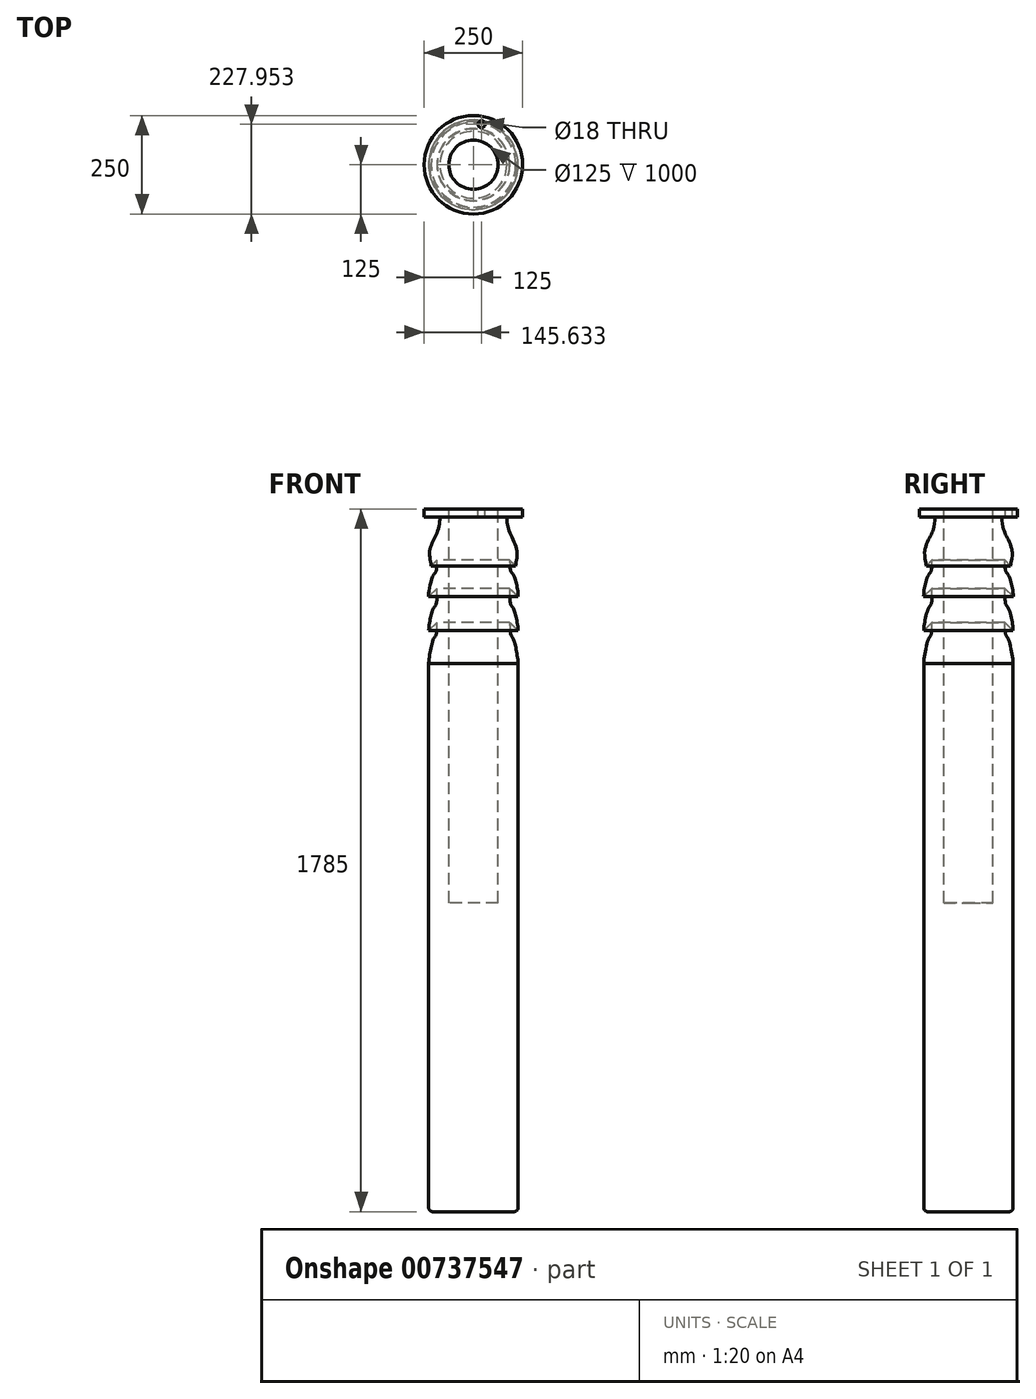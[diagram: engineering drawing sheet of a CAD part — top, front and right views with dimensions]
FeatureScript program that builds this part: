
annotation { "Feature Type Name" : "Feature", "Feature Type Description" : "" }
export const myFeature = defineFeature(function(context is Context, id is Id, definition is map)
    precondition{}
    {
        {
            var Q0;
            Q0=qCreatedBy(makeId("Front.planeOp"),FACE);
            var sketch = newSketch(context, id + "F0", { "sketchPlane" : qUnion([Q0])});
            skLineSegment(sketch, "E0", {"start": v(0, 1000) * mm, "end": v(0, -1000) * mm, "construction": true});
            skLineSegment(sketch, "E1", {"start": v(0, 796) * mm, "end": v(125, 796) * mm});
            skLineSegment(sketch, "E2", {"start": v(125, 796) * mm, "end": v(125, 776) * mm});
            skLineSegment(sketch, "E3", {"start": v(125, 776) * mm, "end": v(85, 776) * mm});
            skFitSpline(sketch, "E4", {"points": [v(85, 776) * mm, v(90.3, 741.64) * mm, v(110.68, 691.75) * mm, v(107.26, 651.86) * mm], "startDerivative": vector(5.14, -104) * mm, "endDerivative": vector(-8.82, -99.6) * mm});
            skFitSpline(sketch, "E5", {"points": [v(92.17, 666.19) * mm, v(100.58, 630.26) * mm, v(113.89, 573.44) * mm], "startDerivative": vector(5.42, -233.9) * mm, "endDerivative": vector(1.67, -111.03) * mm});
            skFitSpline(sketch, "E6", {"points": [v(92.17, 594.06) * mm, v(100.58, 545.8) * mm, v(113.58, 487.63) * mm], "startDerivative": vector(-2.08, -300.06) * mm, "endDerivative": vector(4.8, -112.09) * mm});
            skFitSpline(sketch, "E7", {"points": [v(92.17, 507.95) * mm, v(100.58, 467.82) * mm, v(113.58, 404) * mm], "startDerivative": vector(5.08, -256.5) * mm, "endDerivative": vector(7.87, -118.89) * mm});
            skLineSegment(sketch, "E8", {"start": v(113.58, 487.63) * mm, "end": v(92.17, 507.95) * mm});
            skLineSegment(sketch, "E9", {"start": v(113.89, 573.44) * mm, "end": v(92.17, 594.06) * mm});
            skLineSegment(sketch, "E10", {"start": v(107.26, 651.86) * mm, "end": v(92.17, 666.19) * mm});
            skLineSegment(sketch, "E11", {"start": v(113.58, 404) * mm, "end": v(113.58, -989) * mm});
            skLineSegment(sketch, "E12", {"start": v(113.58, -989) * mm, "end": v(0, -989) * mm});
            skLineSegment(sketch, "E13", {"start": v(0, 796) * mm, "end": v(0, -1000) * mm});
            skSolve(sketch);
        }
        {
            var Q0;
            {var subQ0=sQuery(id+"F0.wireOp",EDGE,"E1");Q0=makeQuery(id+"F0.imprint","IMPRINT",FACE,{"disambiguationData":[TD([[makeQuery(id+"F0.imprint","IMPRINT",EDGE,{"derivedFrom":subQ0}),-1.0]])]});}
            var Q1;
            Q1=sQuery(id+"F0.wireOp",EDGE,"E13");
            revolve(context, id + "F1", {"surfaceOperationType" : NewSurfaceOperationType.NEW, "entities" : qUnion([Q0]), "axis" : qUnion([Q1]), "revolveType" : RevolveType.FULL});
        }
        {
            var Q0;
            Q0=makeQuery(id+"F1.opRevolve","SWEPT_FACE",FACE,{"disambiguationData":[OSD([sQuery(id+"F0.wireOp",EDGE,"E1")])]});
            var sketch = newSketch(context, id + "F2", { "sketchPlane" : qUnion([Q0])});
            skCircle(sketch, "E14", {"center": v(0, 0) * mm, "radius": 105 * mm, "construction": true});
            skCircle(sketch, "E15", {"center": v(20.63, 102.95) * mm, "radius": 9 * mm});
            skSolve(sketch);
        }
        {
            var Q0;
            Q0=makeQuery(id+"F2tzLIQKKAkdXwi_1.1.F2.imprint","IMPRINT",FACE,{"disambiguationData":[TD([[makeQuery(id+"F2tzLIQKKAkdXwi_1.1.F2.imprint","IMPRINT",EDGE,{"derivedFrom":sQuery(id+"F2tzLIQKKAkdXwi_1.1.F2.wireOp",EDGE,"E15")}),1.0]])]});
            var Q1;
            Q1=makeQuery(id+"F2.imprint","IMPRINT",FACE,{"disambiguationData":[TD([[makeQuery(id+"F2.imprint","IMPRINT",EDGE,{"derivedFrom":sQuery(id+"F2.wireOp",EDGE,"E15")}),1.0]])]});
            var Q2;
            Q2=makeQuery(id+"F2tzLIQKKAkdXwi_1.-1.F2.imprint","IMPRINT",FACE,{"disambiguationData":[TD([[makeQuery(id+"F2tzLIQKKAkdXwi_1.-1.F2.imprint","IMPRINT",EDGE,{"derivedFrom":sQuery(id+"F2tzLIQKKAkdXwi_1.-1.F2.wireOp",EDGE,"E15")}),1.0]])]});
            var Q3;
            Q3=makeQuery(id+"F2tzLIQKKAkdXwi_1.-2.F2.imprint","IMPRINT",FACE,{"disambiguationData":[TD([[makeQuery(id+"F2tzLIQKKAkdXwi_1.-2.F2.imprint","IMPRINT",EDGE,{"derivedFrom":sQuery(id+"F2tzLIQKKAkdXwi_1.-2.F2.wireOp",EDGE,"E15")}),1.0]])]});
            var Q4;
            Q4=makeQuery(id+"F2tzLIQKKAkdXwi_1.-3.F2.imprint","IMPRINT",FACE,{"disambiguationData":[TD([[makeQuery(id+"F2tzLIQKKAkdXwi_1.-3.F2.imprint","IMPRINT",EDGE,{"derivedFrom":sQuery(id+"F2tzLIQKKAkdXwi_1.-3.F2.wireOp",EDGE,"E15")}),1.0]])]});
            var Q5;
            Q5=makeQuery(id+"F2tzLIQKKAkdXwi_1.4.F2.imprint","IMPRINT",FACE,{"disambiguationData":[TD([[makeQuery(id+"F2tzLIQKKAkdXwi_1.4.F2.imprint","IMPRINT",EDGE,{"derivedFrom":sQuery(id+"F2tzLIQKKAkdXwi_1.4.F2.wireOp",EDGE,"E15")}),1.0]])]});
            var Q6;
            Q6=makeQuery(id+"F2tzLIQKKAkdXwi_1.3.F2.imprint","IMPRINT",FACE,{"disambiguationData":[TD([[makeQuery(id+"F2tzLIQKKAkdXwi_1.3.F2.imprint","IMPRINT",EDGE,{"derivedFrom":sQuery(id+"F2tzLIQKKAkdXwi_1.3.F2.wireOp",EDGE,"E15")}),1.0]])]});
            var Q7;
            Q7=makeQuery(id+"F2tzLIQKKAkdXwi_1.-6.F2.imprint","IMPRINT",FACE,{"disambiguationData":[TD([[makeQuery(id+"F2tzLIQKKAkdXwi_1.-6.F2.imprint","IMPRINT",EDGE,{"derivedFrom":sQuery(id+"F2tzLIQKKAkdXwi_1.-6.F2.wireOp",EDGE,"E15")}),1.0]])]});
            extrude(context, id + "F3", {"entities" : qUnion([Q0, Q1, Q2, Q3, Q4, Q5, Q6, Q7]), "operationType" : NewBodyOperationType.REMOVE, "endBound" : BoundingType.UP_TO_NEXT, "oppositeDirection" : true, "depth" : 25 * mm, "offsetDistance" : 25 * mm});
        }
        {
            var Q0;
            Q0=makeQuery(id+"F1.opRevolve","SWEPT_FACE",FACE,{"disambiguationData":[OSD([sQuery(id+"F0.wireOp",EDGE,"E1")])]});
            var sketch = newSketch(context, id + "F4", { "sketchPlane" : qUnion([Q0])});
            skCircle(sketch, "E16", {"center": v(0, 0) * mm, "radius": 62.5 * mm});
            skSolve(sketch);
        }
        {
            var Q0;
            Q0=makeQuery(id+"F4.imprint","IMPRINT",FACE,{"disambiguationData":[TD([[makeQuery(id+"F4.imprint","IMPRINT",EDGE,{"derivedFrom":sQuery(id+"F4.wireOp",EDGE,"E16")}),1.0]])]});
            extrude(context, id + "F5", {"entities" : qUnion([Q0]), "operationType" : NewBodyOperationType.REMOVE, "oppositeDirection" : true, "depth" : 1000 * mm, "offsetDistance" : 25 * mm});
        }
        {
            var Q0;
            Q0=makeQuery(id+"F1.opRevolve","SWEPT_EDGE",EDGE,{"disambiguationData":[OSD([sQuery(id+"F0.wireOp",EDGE,"E11"),sQuery(id+"F0.wireOp",EDGE,"E12")])]});
            fillet(context, id + "F6", {"entities" : qUnion([Q0]), "radius" : 10 * mm, "tangentPropagation" : true, "allowEdgeOverflow" : false});
        }
    });
